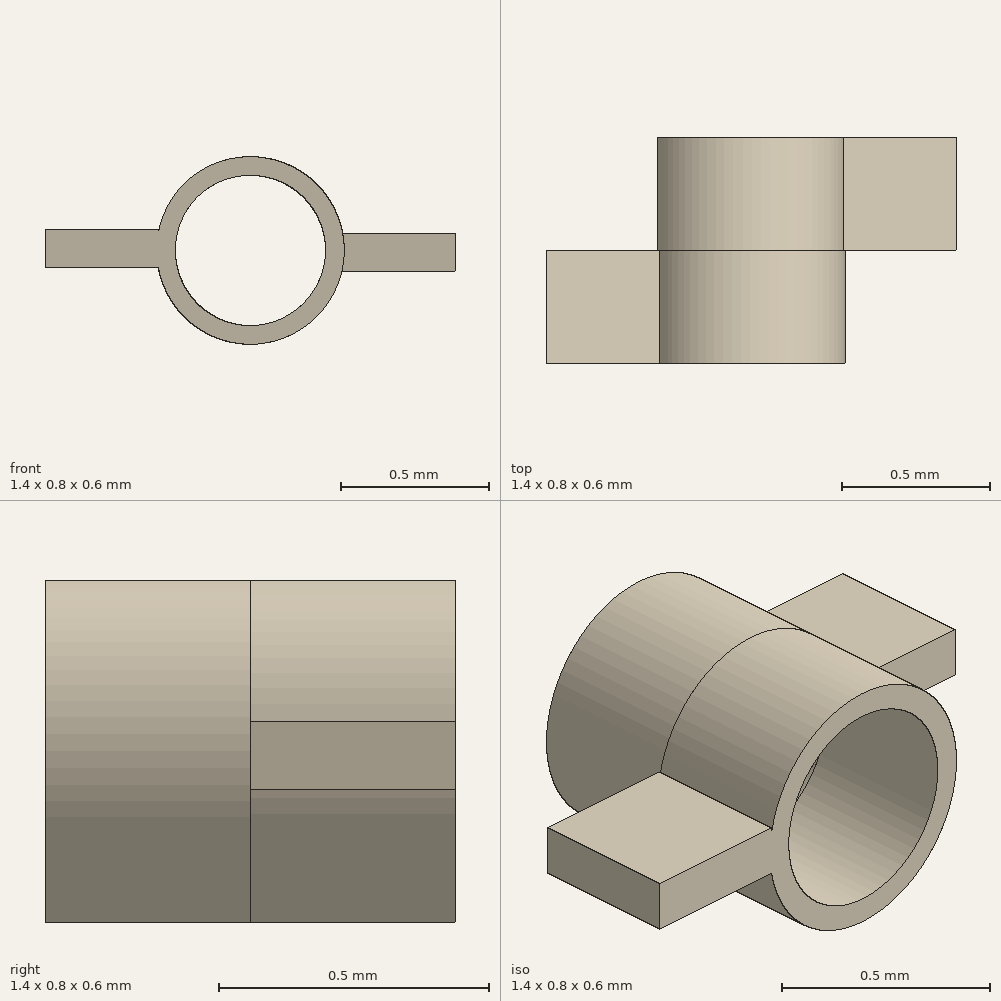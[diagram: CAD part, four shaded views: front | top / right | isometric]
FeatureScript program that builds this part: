
annotation { "Feature Type Name" : "Feature", "Feature Type Description" : "" }
export const myFeature = defineFeature(function(context is Context, id is Id, definition is map)
    precondition{}
    {
        {
            var Q0;
            Q0=qCreatedBy(makeId("Front.planeOp"),FACE);
            var sketch = newSketch(context, id + "F0", { "sketchPlane" : qUnion([Q0])});
            skCircle(sketch, "E0", {"center": v(0, 0) * mm, "radius": 0.32 * mm});
            skCircle(sketch, "E1", {"center": v(0, 0) * mm, "radius": 0.25 * mm});
            skLineSegment(sketch, "E2.bottom", {"start": v(0.31, 0.06) * mm, "end": v(0.7, 0.06) * mm});
            skLineSegment(sketch, "E2.top", {"start": v(0.31, -0.07) * mm, "end": v(0.7, -0.07) * mm});
            skLineSegment(sketch, "E2.left", {"start": v(0.31, 0.06) * mm, "end": v(0.31, -0.07) * mm});
            skLineSegment(sketch, "E2.right", {"start": v(0.7, 0.06) * mm, "end": v(0.7, -0.07) * mm});
            skSolve(sketch);
        }
        {
            var Q0;
            Q0=makeQuery(id+"F0.imprint","IMPRINT",FACE,{"disambiguationData":[TD([[makeQuery(id+"F0.imprint","IMPRINT",EDGE,{"derivedFrom":sQuery(id+"F0.wireOp",EDGE,"E1")}),-1.0]])]});
            var Q1;
            {var subQ0=sQuery(id+"F0.wireOp",EDGE,"E2.left");var subQ1=sQuery(id+"F0.wireOp",EDGE,"E0");var subQ3=makeQuery(id+"F0.imprint","INTERSECT",VERTEX,{"derivedFrom":[subQ1,subQ0]});Q1=makeQuery(id+"F0.imprint","IMPRINT",FACE,{"disambiguationData":[TD([[makeQuery(id+"F0.imprint","IMPRINT",EDGE,{"disambiguationData":[TD([[subQ3,-1.0]])],"derivedFrom":subQ1}),1.0]])]});}
            var Q2;
            {var subQ1=sQuery(id+"F0.wireOp",EDGE,"E2.bottom");Q2=makeQuery(id+"F0.imprint","IMPRINT",FACE,{"disambiguationData":[TD([[makeQuery(id+"F0.imprint","IMPRINT",EDGE,{"derivedFrom":subQ1}),-1.0]])]});}
            extrude(context, id + "F1", {"entities" : qUnion([Q0, Q1, Q2]), "depth" : 0.38 * mm, "offsetDistance" : 25.4 * mm});
        }
        {
            var Q0;
            Q0=makeQuery(id+"F1.opExtrude","SWEPT_BODY",BODY,{"disambiguationData":[OSD([sQuery(id+"F0.wireOp",EDGE,"E0"),sQuery(id+"F0.wireOp",EDGE,"E1"),sQuery(id+"F0.wireOp",EDGE,"E2.bottom"),sQuery(id+"F0.wireOp",EDGE,"E2.top"),sQuery(id+"F0.wireOp",EDGE,"E2.left"),sQuery(id+"F0.wireOp",EDGE,"E2.right")])]});
            var Q1;
            Q1=qCreatedBy(makeId("Front.planeOp"),FACE);
            mirror(context, id + "F2", {"entities" : qUnion([Q0]), "mirrorPlane" : qUnion([Q1])});
        }
        {
            var Q0;
            Q0=makeQuery(id+"F1.opExtrude","SWEPT_BODY",BODY,{"disambiguationData":[OSD([sQuery(id+"F0.wireOp",EDGE,"E0"),sQuery(id+"F0.wireOp",EDGE,"E1"),sQuery(id+"F0.wireOp",EDGE,"E2.bottom"),sQuery(id+"F0.wireOp",EDGE,"E2.top"),sQuery(id+"F0.wireOp",EDGE,"E2.left"),sQuery(id+"F0.wireOp",EDGE,"E2.right")])]});
            var Q1;
            Q1=makeQuery(id+"F2.opPattern","COPY",FACE,{"derivedFrom":makeQuery(id+"F1.opExtrude","SWEPT_FACE",FACE,{"disambiguationData":[OSD([sQuery(id+"F0.wireOp",EDGE,"E0")])]}),"instanceName":"1"});
            transform(context, id + "F3", {"entities" : qUnion([Q0]), "transformType" : TransformType.ROTATION, "transformAxis" : qUnion([Q1]), "angle" : 180 * degree, "makeCopy" : false});
        }
    });
